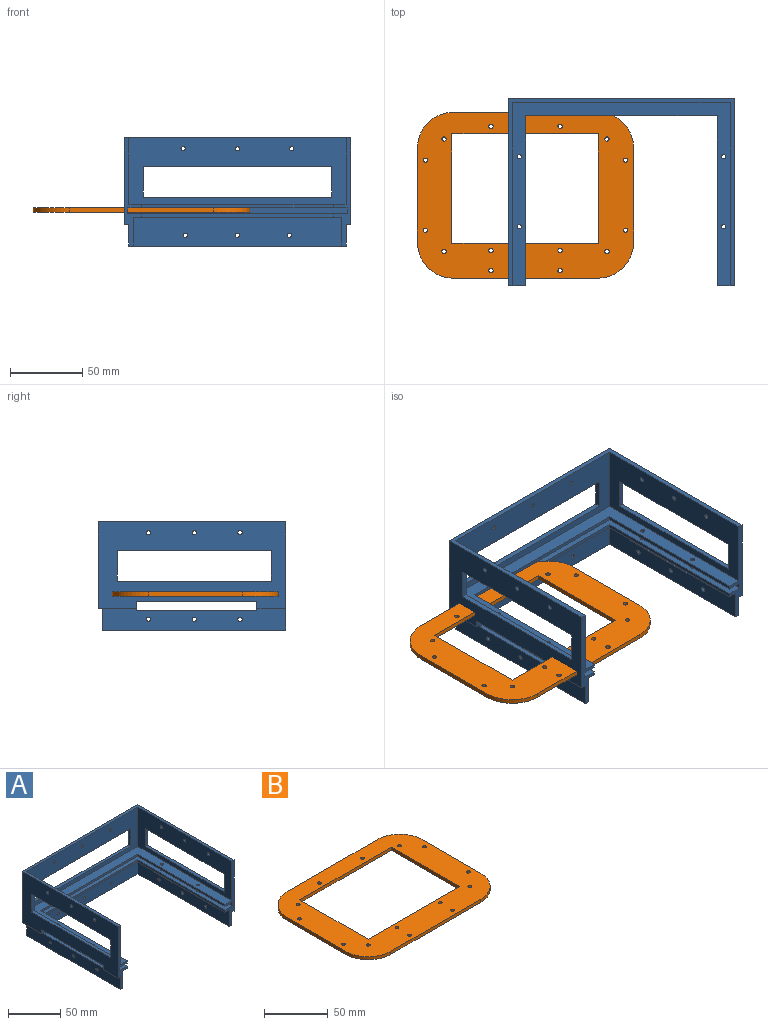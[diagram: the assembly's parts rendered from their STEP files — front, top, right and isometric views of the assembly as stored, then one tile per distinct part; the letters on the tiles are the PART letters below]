
ASSEMBLY  parts=2 mates=2
PART A: 84 faces, bbox 157x130x75 mm
  f0: plane 157x26.4mm, normal (0,0,-1), area 650.9mm2, adj f4,f7,f13,f31,f32,f33,f76,f81
  f1: plane 20x3.2mm, normal (0,0,-1), area 64mm2, adj f7,f16,f32,f78
  f2: plane 123.6x20mm, normal (-1,0,0), area 1907.4mm2, adj f8,f16,f34,f35,f47,f48,f49,f76
  f3: plane 123.6x20mm, normal (1,0,0), area 1907.4mm2, adj f8,f9,f34,f35,f44,f45,f46,f79
  f4: plane 130.01x60.01mm, normal (-1,0,0), area 5118.2mm2, adj f0,f8,f9,f13,f15,f17,f40,f41
  f5: plane 126.8x46mm, normal (1,0,0), area 3568.8mm2, adj f9,f14,f17,f22,f40,f41,f42,f43
  f6: plane 126.8x46mm, normal (-1,0,0), area 3568.8mm2, adj f14,f16,f17,f22,f36,f37,f38,f39
  f7: plane 130.01x60.01mm, normal (1,0,0), area 5118.2mm2, adj f0,f1,f8,f13,f16,f17,f36,f37
  f8: plane 157x123.6mm, normal (0,0,-1), area 3207.1mm2, adj f2,f3,f4,f7,f9,f11,f16,f23
  f9: plane 75x12.2mm, normal (0,-1,0), area 298.2mm2, adj f3,f4,f5,f8,f10,f15,f17,f22
  f10: plane 117.8x2.5mm, normal (1,0,0), area 294.5mm2, adj f9,f22,f24,f26
  f11: plane 132.6x2.5mm, normal (0,-1,0), area 331.5mm2, adj f8,f23,f25,f30
  f12: plane 117.8x2.5mm, normal (-1,0,0), area 294.5mm2, adj f16,f22,f24,f26
  f13: plane 157x60mm, normal (0,1,0), area 6656.2mm2, adj f0,f4,f7,f17,f18,f19,f20,f21
  f14: plane 150.6x46mm, normal (0,-1,0), area 4163.8mm2, adj f5,f6,f17,f18,f19,f20,f21,f22
  f15: plane 20x3.2mm, normal (0,0,-1), area 64mm2, adj f4,f9,f31,f79
  f16: plane 75x12.2mm, normal (0,-1,0), area 298.2mm2, adj f1,f2,f6,f7,f8,f12,f17,f22
  f17: plane 157x130mm, normal (0,0,1), area 1313.9mm2, adj f4,f5,f6,f7,f9,f13,f14,f16
  f18: plane 130.6x3.2mm, normal (0,0,-1), area 417.9mm2, adj f13,f14,f19,f21
  f19: plane 21x3.2mm, normal (1,0,0), area 67.2mm2, adj f13,f14,f18,f20
  f20: plane 130.6x3.2mm, normal (0,0,1), area 417.9mm2, adj f13,f14,f19,f21
  f21: plane 21x3.2mm, normal (-1,0,0), area 67.2mm2, adj f13,f14,f18,f20
  f22: plane 150.6x126.8mm, normal (0,0,1), area 3447.5mm2, adj f5,f6,f9,f10,f12,f14,f16,f24
  f23: plane 117.8x2.5mm, normal (1,0,0), area 294.5mm2, adj f8,f9,f11,f30
  f24: plane 132.6x2.5mm, normal (0,-1,0), area 331.5mm2, adj f10,f12,f22,f26
  f25: plane 117.8x2.5mm, normal (-1,0,0), area 294.5mm2, adj f8,f11,f16,f30
  f26: plane 152x127.5mm, normal (0,0,-1), area 3731.4mm2, adj f9,f10,f12,f16,f24,f27,f28,f29
  f27: plane 152x4mm, normal (0,-1,0), area 608mm2, adj f26,f28,f29,f30
  f28: plane 127.5x4mm, normal (1,0,0), area 510mm2, adj f9,f26,f27,f30
  f29: plane 127.5x4mm, normal (-1,0,0), area 510mm2, adj f16,f26,f27,f30
  f30: plane 152x127.5mm, normal (0,0,1), area 3731.4mm2, adj f9,f11,f16,f23,f25,f27,f28,f29
  f31: plane 126.8x15mm, normal (-1,0,0), area 1755.4mm2, adj f0,f9,f15,f33,f34,f44,f45,f46
  f32: plane 126.8x15mm, normal (1,0,0), area 1755.4mm2, adj f0,f1,f16,f33,f34,f47,f48,f49
  f33: plane 150.6x15mm, normal (0,1,0), area 2237.8mm2, adj f0,f31,f32,f34,f71,f72,f73
  f34: plane 150.6x126.8mm, normal (0,0,-1), area 1273mm2, adj f2,f3,f9,f16,f31,f32,f33,f35
  f35: plane 144.2x20mm, normal (0,-1,0), area 2862.8mm2, adj f2,f3,f8,f34,f71,f72,f73
  f36: plane 106.8x3.2mm, normal (0,0,-1), area 341.8mm2, adj f6,f7,f37,f39
  f37: plane 21x3.2mm, normal (0,-1,0), area 67.2mm2, adj f6,f7,f36,f38
  f38: plane 106.8x3.2mm, normal (0,0,1), area 341.8mm2, adj f6,f7,f37,f39
  f39: plane 21x3.2mm, normal (0,1,0), area 67.2mm2, adj f6,f7,f36,f38
  f40: plane 106.8x3.2mm, normal (0,0,-1), area 341.8mm2, adj f4,f5,f41,f43
  f41: plane 21x3.2mm, normal (0,1,0), area 67.2mm2, adj f4,f5,f40,f42
  f42: plane 106.8x3.2mm, normal (0,0,1), area 341.8mm2, adj f4,f5,f41,f43
  f43: plane 21x3.2mm, normal (0,-1,0), area 67.2mm2, adj f4,f5,f40,f42
  f44: cylinder r=1.5mm len=3.2mm, axis (-1,0,0), area 30.2mm2, adj f3,f31
  f45: cylinder r=1.5mm len=3.2mm, axis (-1,0,0), area 30.2mm2, adj f3,f31
  f46: cylinder r=1.5mm len=3.2mm, axis (-1,0,0), area 30.2mm2, adj f3,f31
  f47: cylinder r=1.5mm len=3.2mm, axis (1,0,0), area 30.2mm2, adj f2,f32
  f48: cylinder r=1.5mm len=3.2mm, axis (1,0,0), area 30.2mm2, adj f2,f32
  f49: cylinder r=1.5mm len=3.2mm, axis (1,0,0), area 30.2mm2, adj f2,f32
  f50: cylinder r=1.5mm len=3.2mm, axis (1,0,0), area 30.2mm2, adj f4,f5
  f51: cylinder r=1.5mm len=3.2mm, axis (1,0,0), area 30.2mm2, adj f4,f5
  f52: cylinder r=1.5mm len=3.2mm, axis (1,0,0), area 30.2mm2, adj f4,f5
  f53: cylinder r=1.5mm len=3.2mm, axis (0,-1,0), area 30.2mm2, adj f13,f14
  f54: cylinder r=1.5mm len=3.2mm, axis (0,-1,0), area 30.2mm2, adj f13,f14
  f55: cylinder r=1.5mm len=3.2mm, axis (0,-1,0), area 30.2mm2, adj f13,f14
  f56: cylinder r=1.5mm len=3.2mm, axis (-1,0,0), area 30.2mm2, adj f6,f7
  f57: cylinder r=1.5mm len=3.2mm, axis (-1,0,0), area 30.2mm2, adj f6,f7
  f58: cylinder r=1.5mm len=3.2mm, axis (-1,0,0), area 30.2mm2, adj f6,f7
  f59: cone r=0mm half-angle=59deg, axis (0,0,1), area 0.2mm2, adj f60,f82
  f60: cylinder r=1.5mm len=3mm, axis (0,0,1), area 23.6mm2, adj f8,f30,f59
  f61: cone r=0mm half-angle=59deg, axis (0,0,1), area 0.2mm2, adj f62,f83
  f62: cylinder r=1.5mm len=3mm, axis (0,0,1), area 23.6mm2, adj f8,f30,f61
  f63: cone r=0mm half-angle=59deg, axis (0,0,1), area 0.2mm2, adj f64,f74
  f64: cylinder r=1.5mm len=3mm, axis (0,0,1), area 23.6mm2, adj f8,f30,f63
  f65: cone r=0mm half-angle=59deg, axis (0,0,1), area 0.2mm2, adj f66,f75
  f66: cylinder r=1.5mm len=3mm, axis (0,0,1), area 23.6mm2, adj f8,f30,f65
  f67: cylinder r=1.5mm len=3mm, axis (0,0,1), area 23.6mm2, adj f22,f26
  f68: cylinder r=1.5mm len=3mm, axis (0,0,1), area 23.6mm2, adj f22,f26
  f69: cylinder r=1.5mm len=3mm, axis (0,0,1), area 23.6mm2, adj f22,f26
  f70: cylinder r=1.5mm len=3mm, axis (0,0,1), area 23.6mm2, adj f22,f26
  f71: cylinder r=1.5mm len=3.2mm, axis (0,-1,0), area 30.2mm2, adj f33,f35
  f72: cylinder r=1.5mm len=3.2mm, axis (0,-1,0), area 30.2mm2, adj f33,f35
  f73: cylinder r=1.5mm len=3.2mm, axis (0,-1,0), area 30.2mm2, adj f33,f35
  f74: extruded ~6.4x1.5mm, area 9.7mm2, adj f7,f8,f63
  f75: extruded ~6.4x1.5mm, area 9.7mm2, adj f7,f8,f65
  f76: plane 6.5x6.4mm, normal (0,-1,0), area 36.8mm2, adj f0,f2,f7,f8,f32,f77
  f77: plane 83.6x3.2mm, normal (0,0,1), area 267.5mm2, adj f2,f32,f76,f78
  f78: plane 6.5x6.4mm, normal (0,1,0), area 36.8mm2, adj f1,f2,f7,f8,f32,f77
  f79: plane 6.5x6.4mm, normal (0,1,0), area 36.8mm2, adj f3,f4,f8,f15,f31,f80
  f80: plane 83.6x3.2mm, normal (0,0,1), area 267.5mm2, adj f3,f31,f79,f81
  f81: plane 6.5x6.4mm, normal (0,-1,0), area 36.8mm2, adj f0,f3,f4,f8,f31,f80
  f82: extruded ~6.4x1.5mm, area 9.7mm2, adj f4,f8,f59
  f83: extruded ~6.4x1.5mm, area 9.7mm2, adj f4,f8,f61
PART B: 28 faces, bbox 150x115x3 mm
  f0: plane 150x115mm, normal (0,0,-1), area 8915.8mm2, adj f2,f3,f4,f5,f6,f7,f8,f9
  f1: plane 150x115mm, normal (0,0,1), area 8915.8mm2, adj f2,f3,f4,f5,f6,f7,f8,f9
  f2: cylinder r=25mm len=25mm, axis (0,0,-1), area 117.8mm2, adj f0,f1,f3,f9
  f3: plane 100x3mm, normal (0,1,0), area 300mm2, adj f0,f1,f2,f4
  f4: cylinder r=25mm len=25mm, axis (0,0,-1), area 117.8mm2, adj f0,f1,f3,f5
  f5: plane 65x3mm, normal (-1,0,0), area 195mm2, adj f0,f1,f4,f6
  f6: cylinder r=25mm len=25mm, axis (0,0,-1), area 117.8mm2, adj f0,f1,f5,f7
  f7: plane 100x3mm, normal (0,-1,0), area 300mm2, adj f0,f1,f6,f8
  f8: cylinder r=25mm len=25mm, axis (0,0,-1), area 117.8mm2, adj f0,f1,f7,f9
  f9: plane 65x3mm, normal (1,0,0), area 195mm2, adj f0,f1,f2,f8
  f10: cylinder r=1.5mm len=3mm, axis (0,0,-1), area 28.3mm2, adj f0,f1
  f11: cylinder r=1.5mm len=3mm, axis (0,0,-1), area 28.3mm2, adj f0,f1
  f12: cylinder r=1.5mm len=3mm, axis (0,0,-1), area 28.3mm2, adj f0,f1
  f13: cylinder r=1.5mm len=3mm, axis (0,0,-1), area 28.3mm2, adj f0,f1
  f14: cylinder r=1.5mm len=3mm, axis (0,0,-1), area 28.3mm2, adj f0,f1
  f15: cylinder r=1.5mm len=3mm, axis (0,0,-1), area 28.3mm2, adj f0,f1
  f16: cylinder r=1.5mm len=3mm, axis (0,0,-1), area 28.3mm2, adj f0,f1
  f17: cylinder r=1.5mm len=3mm, axis (0,0,-1), area 28.3mm2, adj f0,f1
  f18: plane 101.5x3mm, normal (0,-1,0), area 304.5mm2, adj f0,f1,f19,f21
  f19: plane 75.85x3mm, normal (1,0,0), area 227.5mm2, adj f0,f1,f18,f20
  f20: plane 101.5x3mm, normal (0,1,0), area 304.5mm2, adj f0,f1,f19,f21
  f21: plane 75.85x3mm, normal (-1,0,0), area 227.5mm2, adj f0,f1,f18,f20
  f22: cylinder r=1.5mm len=3mm, axis (0,0,1), area 28.3mm2, adj f0,f1
  f23: cylinder r=1.5mm len=3mm, axis (0,0,1), area 28.3mm2, adj f0,f1
  f24: cylinder r=1.5mm len=3mm, axis (0,0,1), area 28.3mm2, adj f0,f1
  f25: cylinder r=1.5mm len=3mm, axis (0,0,1), area 28.3mm2, adj f0,f1
  f26: cylinder r=1.5mm len=3mm, axis (0,0,1), area 28.3mm2, adj f0,f1
  f27: cylinder r=1.5mm len=3mm, axis (0,0,1), area 28.3mm2, adj f0,f1
PLACE A t=(-12.3,-24.36,56.26)mm
PLACE B t=(-78.81,-26.57,4.76)mm
MATE parallel B.f1 <-> A.f26  axis (0,0,1) through (-78.6,-30.46,7.76)mm
MATE fastened B.f1 <-> A.f26  axis (0,0,1) through (-78.6,-30.46,7.76)mm
